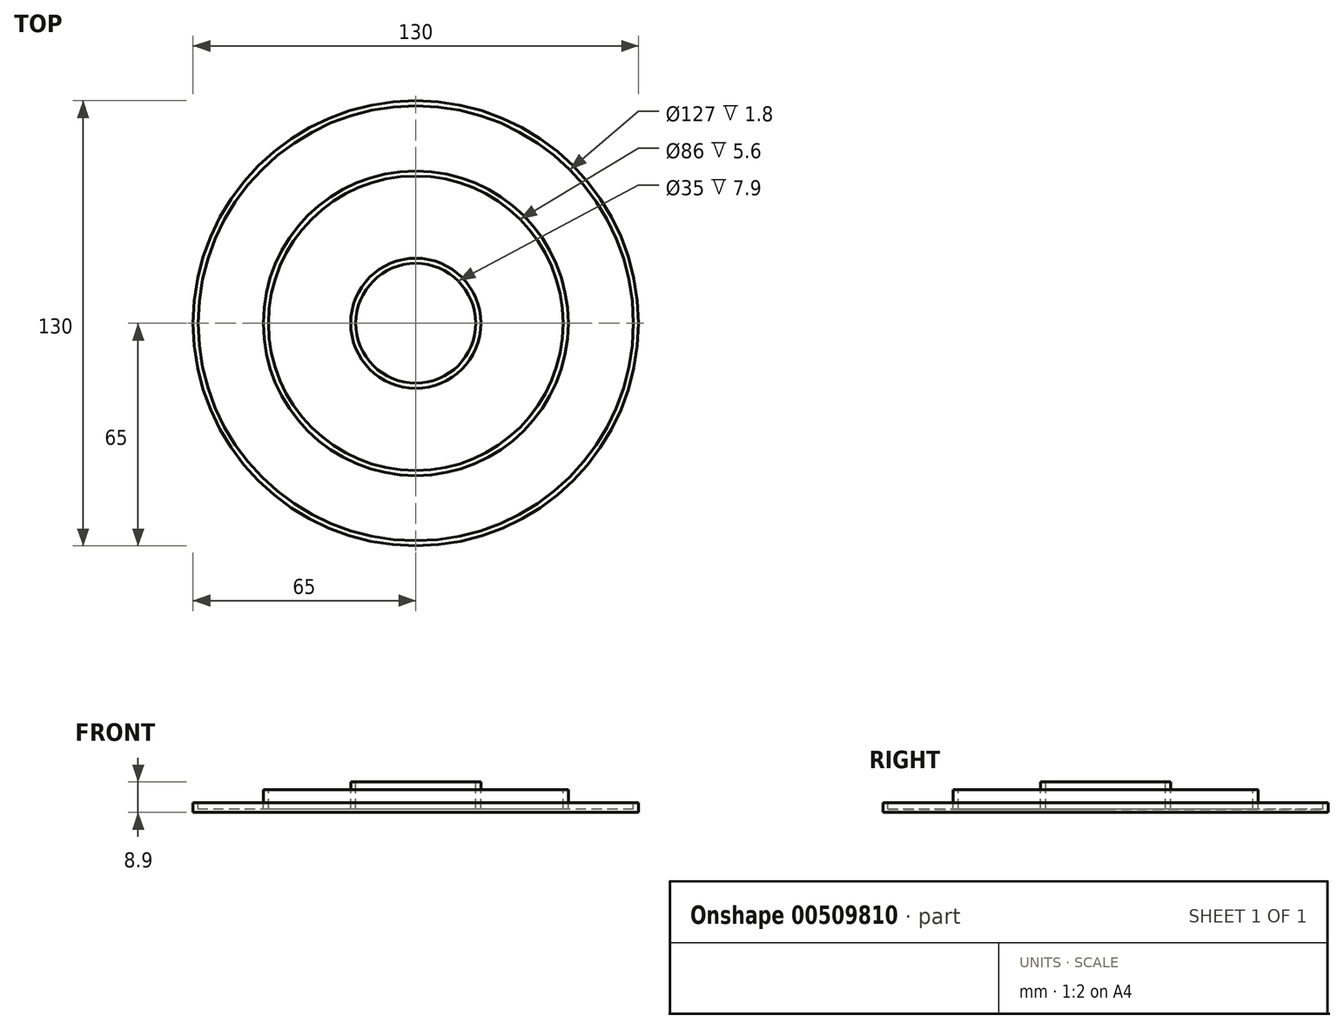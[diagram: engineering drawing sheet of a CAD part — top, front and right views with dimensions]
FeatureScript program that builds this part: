
annotation { "Feature Type Name" : "Feature", "Feature Type Description" : "" }
export const myFeature = defineFeature(function(context is Context, id is Id, definition is map)
    precondition{}
    {
        {
            var Q0;
            Q0=qCreatedBy(makeId("Front.planeOp"),FACE);
            var sketch = newSketch(context, id + "F0", { "sketchPlane" : qUnion([Q0])});
            skLineSegment(sketch, "E0", {"start": v(0, 6.5) * mm, "end": v(65, 6.5) * mm});
            skLineSegment(sketch, "E1", {"start": v(65, 6.51) * mm, "end": v(65, 9.31) * mm});
            skLineSegment(sketch, "E2", {"start": v(65, 9.3) * mm, "end": v(63.5, 9.3) * mm});
            skLineSegment(sketch, "E3", {"start": v(63.5, 9.31) * mm, "end": v(63.5, 7.51) * mm});
            skLineSegment(sketch, "E4", {"start": v(63.5, 7.51) * mm, "end": v(44.5, 7.5) * mm});
            skLineSegment(sketch, "E5", {"start": v(44.5, 7.51) * mm, "end": v(44.5, 13.11) * mm});
            skLineSegment(sketch, "E6", {"start": v(44.5, 13.1) * mm, "end": v(43, 13.1) * mm});
            skLineSegment(sketch, "E7", {"start": v(43, 13.1) * mm, "end": v(43, 7.51) * mm});
            skLineSegment(sketch, "E8", {"start": v(43, 7.51) * mm, "end": v(19, 7.5) * mm});
            skLineSegment(sketch, "E9", {"start": v(19, 7.5) * mm, "end": v(19, 15.41) * mm});
            skLineSegment(sketch, "E10", {"start": v(19, 15.41) * mm, "end": v(17.5, 15.41) * mm});
            skLineSegment(sketch, "E11", {"start": v(17.5, 15.41) * mm, "end": v(17.5, 7.51) * mm});
            skLineSegment(sketch, "E12", {"start": v(17.5, 7.51) * mm, "end": v(0, 7.51) * mm});
            skLineSegment(sketch, "E13", {"start": v(0, 7.51) * mm, "end": v(0, 6.5) * mm});
            skSolve(sketch);
        }
        {
            var Q0;
            Q0 = qSketchRegion(id + "F0", true);
            var Q1;
            Q1=sQuery(id+"F0.wireOp",EDGE,"E13");
            revolve(context, id + "F1", {"entities" : qUnion([Q0]), "axis" : qUnion([Q1]), "revolveType" : RevolveType.FULL});
        }
    });
